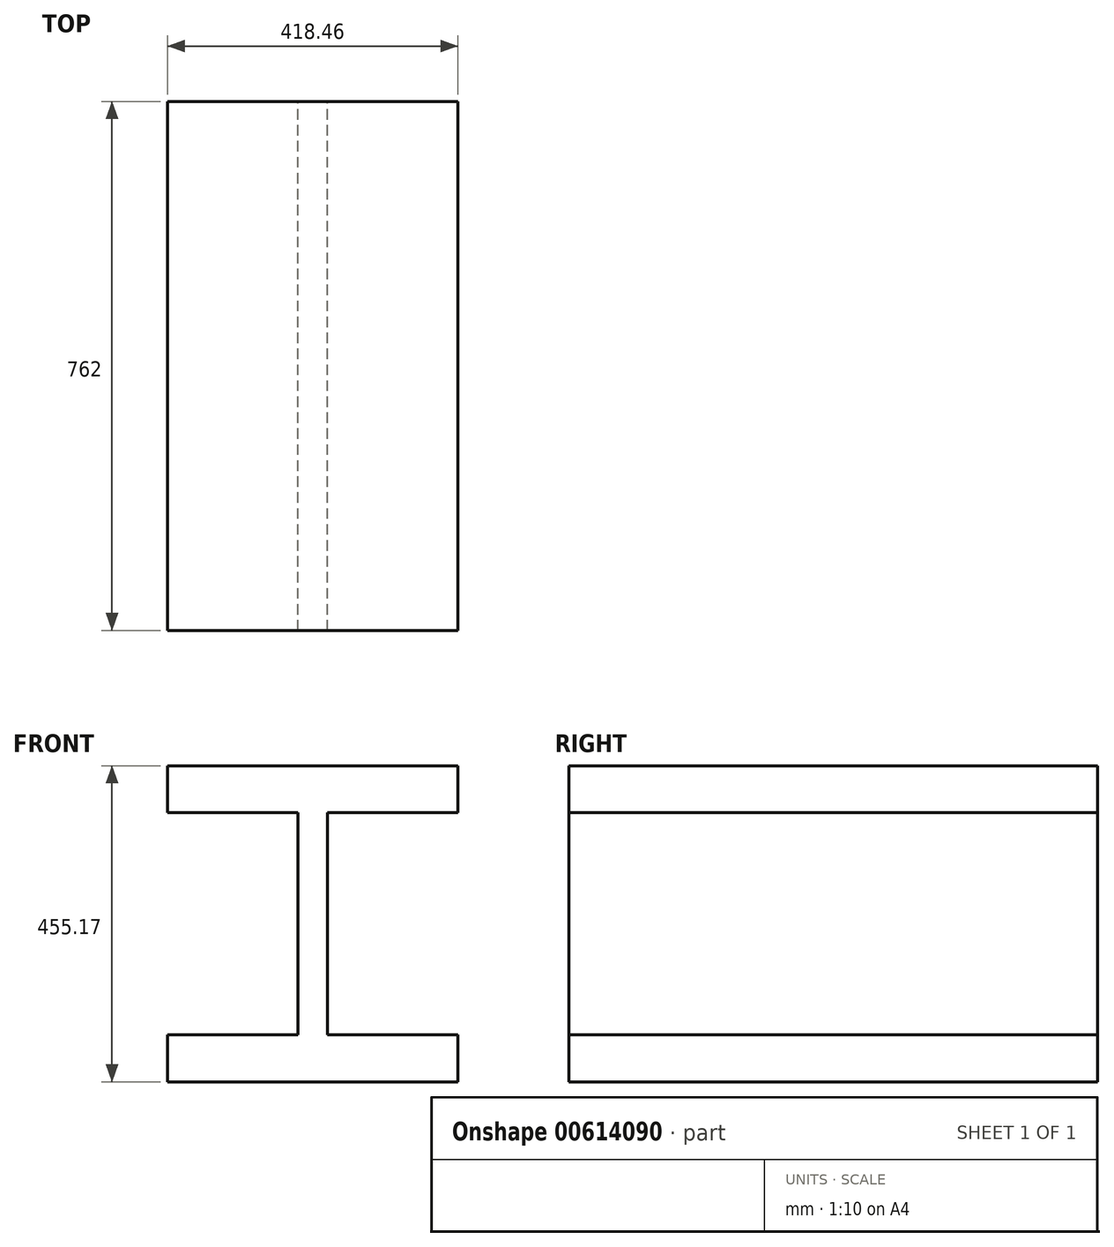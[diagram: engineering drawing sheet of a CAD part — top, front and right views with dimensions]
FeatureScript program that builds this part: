
annotation { "Feature Type Name" : "Feature", "Feature Type Description" : "" }
export const myFeature = defineFeature(function(context is Context, id is Id, definition is map)
    precondition{}
    {
        {
            var Q0;
            Q0=qCreatedBy(makeId("Front.planeOp"),FACE);
            var sketch = newSketch(context, id + "F0", { "sketchPlane" : qUnion([Q0])});
            skLineSegment(sketch, "E0", {"start": v(0, 0) * mm, "end": v(-223.12, 0) * mm});
            skLineSegment(sketch, "E1", {"start": v(-223.12, 0) * mm, "end": v(-223.12, -67.56) * mm});
            skLineSegment(sketch, "E2", {"start": v(-223.12, -67.56) * mm, "end": v(-34.9, -67.56) * mm});
            skLineSegment(sketch, "E3", {"start": v(-34.9, -67.56) * mm, "end": v(-34.9, -387.6) * mm});
            skLineSegment(sketch, "E4", {"start": v(-34.9, -387.6) * mm, "end": v(-223.12, -387.6) * mm});
            skLineSegment(sketch, "E5", {"start": v(-223.12, -387.6) * mm, "end": v(-223.12, -455.17) * mm});
            skLineSegment(sketch, "E6", {"start": v(-223.12, -455.17) * mm, "end": v(195.34, -455.17) * mm});
            skLineSegment(sketch, "E7", {"start": v(195.34, -455.17) * mm, "end": v(195.34, -387.6) * mm});
            skLineSegment(sketch, "E8", {"start": v(195.34, -387.6) * mm, "end": v(7.13, -387.6) * mm});
            skLineSegment(sketch, "E9", {"start": v(7.13, -387.6) * mm, "end": v(7.13, -67.56) * mm});
            skLineSegment(sketch, "E10", {"start": v(7.13, -67.56) * mm, "end": v(195.34, -67.56) * mm});
            skLineSegment(sketch, "E11", {"start": v(195.34, -67.56) * mm, "end": v(195.34, 0) * mm});
            skLineSegment(sketch, "E12", {"start": v(195.34, 0) * mm, "end": v(0, 0) * mm});
            skSolve(sketch);
        }
        {
            var Q0;
            Q0 = qSketchRegion(id + "F0", true);
            extrude(context, id + "F1", {"entities" : qUnion([Q0]), "depth" : 762 * mm, "offsetDistance" : 25.4 * mm});
        }
    });
